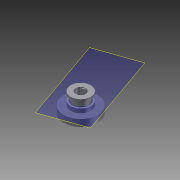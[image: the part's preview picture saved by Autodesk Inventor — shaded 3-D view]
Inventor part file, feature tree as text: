
AUTODESK INVENTOR PART (.ipt)
format: ipt  version: 2012 (Build 160160000, 160)  size: 739,840 bytes
history: native  units: mm
features: extrude x9, sketch x9, other x3, plane x3, projected_geometry x1, reference x1
ambient origin geometry x8: Origin, YZ Plane, XZ Plane, XY Plane, X Axis, Y Axis, Z Axis, Center Point
bodies: Solid1 (feature_tree)
feature tree (26):
  other  "Spur Gear2"
  extrude  "Extrusion1"  Depth=10.0mm TaperAngle=0.0deg
  extrude  "Extrusion2"  Depth=3.570646mm
  extrude  "Extrusion3"  Depth=0.3mm
  plane  "Work Plane1"
  extrude  "Extrusion4"  Depth=2.0mm
  extrude  "Extrusion5"  Depth=1.0mm
  extrude  "Extrusion6"  Depth=0.3mm TaperAngle=0.0deg
  sketch  "Sketch8"  dims[d18=0.5mm d19=0.0mm d20=10.0mm d21=0.0mm]
  plane  "Work Plane2"
  extrude  "Extrusion7"  Depth=10.0mm TaperAngle=0.0deg
  extrude  "Extrusion8"  Depth=0.3mm TaperAngle=0.0deg
  sketch  "Sketch10"  dims[d26=22.5mm]
  plane  "Work Plane3"
  extrude  "Extrusion9"  [1 undecoded]
  other  "Solid1::Spur Gear2"
  other  "TaggingFeature1"
  sketch  "Sketch2"  dims[d0=10.0mm d1=10.0mm d2=0.0mm]
  projected_geometry  "Projected Loop1"
  sketch  "Sketch3"  dims[d3=6.0mm d4=3.570646mm]
  sketch  "Sketch4"  dims[d6=0.3mm d7=0.3mm]
  sketch  "Sketch5"  dims[d8=10.0mm d9=0.0mm d10=2.0mm]
  reference  "Reference1"
  sketch  "Sketch6"  dims[d11=8.0mm d12=0.0mm d13=1.0mm]
  sketch  "Sketch7"  dims[d14=3.0mm d15=0.0mm d16=0.3mm d17=0.0mm]
  sketch  "Sketch9"  dims[d22=0.3mm d23=0.0mm d24=0.3mm d25=0.0mm]
note: 1 required parameter value undecoded (feature->parameter linkage not recoverable at this tier; creation-order binding heuristic only, values carry confidence <= 0.55)
